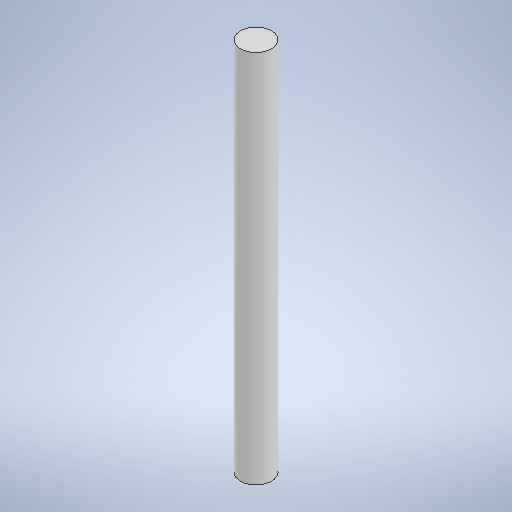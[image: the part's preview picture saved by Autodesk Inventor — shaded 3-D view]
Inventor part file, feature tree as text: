
AUTODESK INVENTOR PART (.ipt)
format: ipt  version: 2025.2 (Build 292293000, 293)  size: 228,352 bytes
history: native  units: mm
features: extrude x1, sketch x1
ambient origin geometry x8: Origin, YZ Plane, XZ Plane, XY Plane, X Axis, Y Axis, Z Axis, Center Point
bodies: Solid1 (feature_tree)
feature tree (2):
  extrude  "Extrusion1"  Depth=36.0mm TaperAngle=0.0deg
  sketch  "Sketch1"  dims[d0=3.0mm d1=36.0mm d2=0.0mm]
